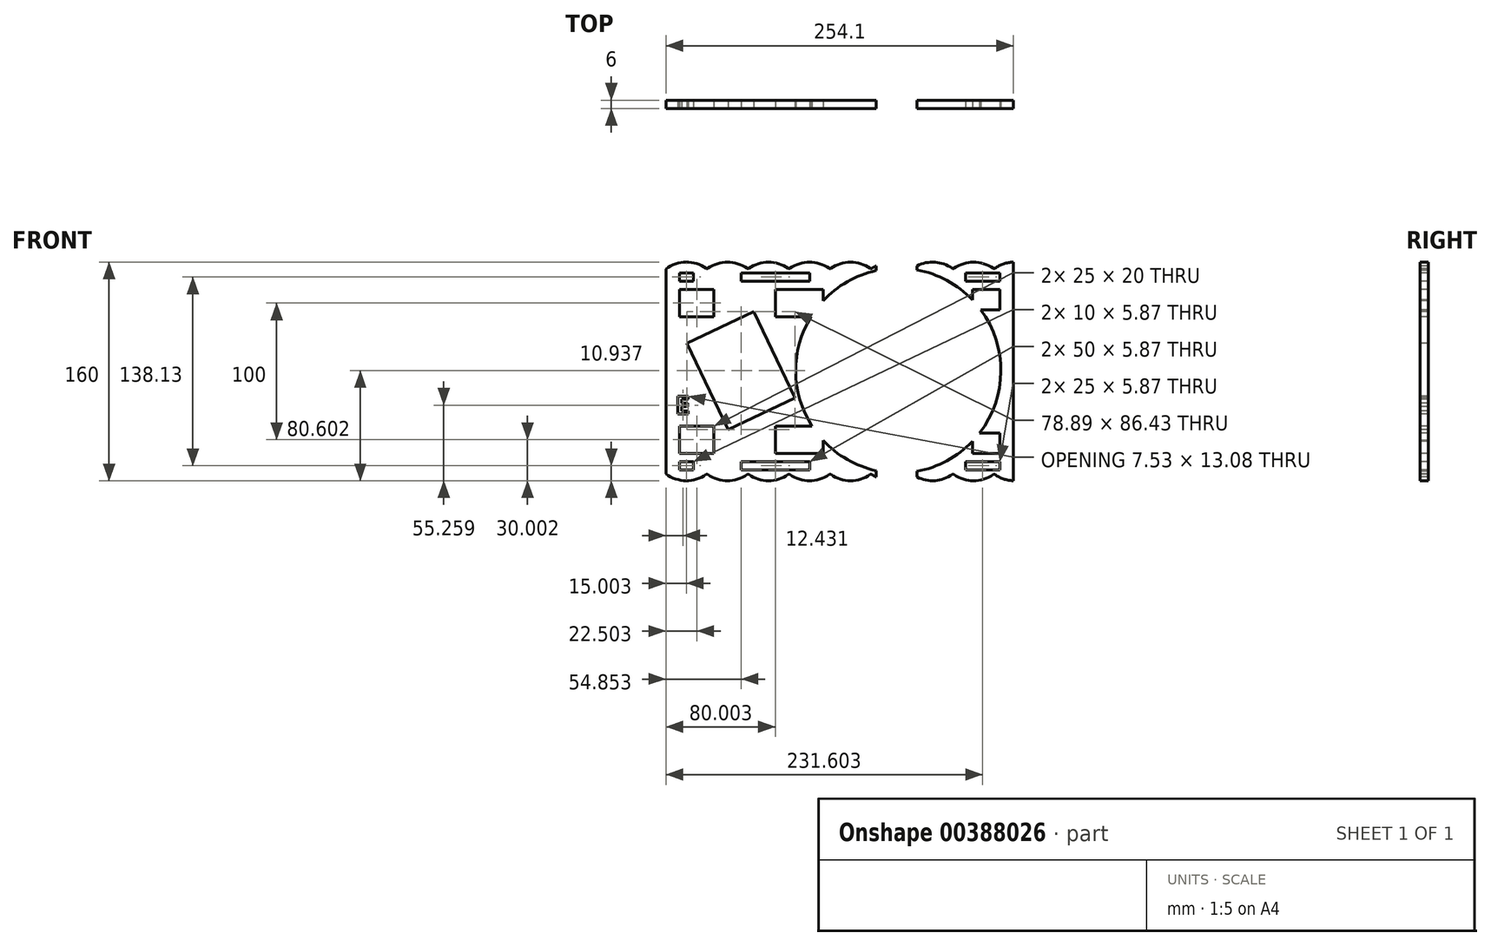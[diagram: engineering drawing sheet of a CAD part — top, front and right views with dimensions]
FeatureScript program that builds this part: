
annotation { "Feature Type Name" : "Feature", "Feature Type Description" : "" }
export const myFeature = defineFeature(function(context is Context, id is Id, definition is map)
    precondition{}
    {
        {
            var Q0;
            Q0=qCreatedBy(makeId("Front.planeOp"),FACE);
            var sketch = newSketch(context, id + "F0", { "sketchPlane" : qUnion([Q0])});
            skCircle(sketch, "E0", {"center": v(28.93, 18.7) * mm, "radius": 75 * mm});
            skPoint(sketch, "E0.first.point", {"position": v(-5.87, 85.13) * mm});
            skPoint(sketch, "E0.second.point", {"position": v(-5.87, -47.74) * mm});
            skPoint(sketch, "E0.second.point.positionSnap0", {"position": v(-5.87, 85.13) * mm});
            skPoint(sketch, "E0.third.point", {"position": v(103.85, 15.25) * mm});
            skLineSegment(sketch, "E1.0", {"start": v(-76.83, 61.9) * mm, "end": v(-125.56, 38.65) * mm});
            skLineSegment(sketch, "E2.0", {"start": v(-46.67, -1.26) * mm, "end": v(-76.83, 61.9) * mm});
            skLineSegment(sketch, "E3.0", {"start": v(-95.4, -24.52) * mm, "end": v(-46.67, -1.26) * mm});
            skLineSegment(sketch, "E4.0", {"start": v(-125.56, 38.65) * mm, "end": v(-95.4, -24.52) * mm});
            skLineSegment(sketch, "E5", {"start": v(-140.97, 101.1) * mm, "end": v(-140.97, 90.01) * mm, "construction": true});
            skLineSegment(sketch, "E6", {"start": v(-133.24, 98.1) * mm, "end": v(-149.42, 98.1) * mm, "construction": true});
            skLineSegment(sketch, "E7.0", {"start": v(76.35, -61.9) * mm, "end": v(117.62, -61.9) * mm, "construction": true});
            skLineSegment(sketch, "E8.0", {"start": v(113.13, 16.1) * mm, "end": v(113.13, -65.37) * mm, "construction": true});
            skLineSegment(sketch, "E9.bottom", {"start": v(-140.97, 98.1) * mm, "end": v(113.13, 98.1) * mm});
            skLineSegment(sketch, "E9.top", {"start": v(-140.97, -61.9) * mm, "end": v(113.13, -61.9) * mm});
            skLineSegment(sketch, "E9.left", {"start": v(-140.97, 98.1) * mm, "end": v(-140.97, -61.9) * mm});
            skLineSegment(sketch, "E9.right", {"start": v(113.13, 98.1) * mm, "end": v(113.13, -61.9) * mm});
            skLineSegment(sketch, "E10", {"start": v(-140.97, 18.1) * mm, "end": v(113.13, 18.1) * mm, "construction": true});
            skLineSegment(sketch, "E11", {"start": v(-76.83, 61.9) * mm, "end": v(-95.4, -24.52) * mm, "construction": true});
            skLineSegment(sketch, "E12", {"start": v(-125.56, 38.65) * mm, "end": v(-46.67, -1.26) * mm, "construction": true});
            skPoint(sketch, "E13", {"position": v(-86.12, 18.7) * mm});
            skCircle(sketch, "E14", {"center": v(-86.12, 18.7) * mm, "radius": 27 * mm, "construction": true});
            skSolve(sketch);
        }
        {
            var Q0;
            Q0=qCreatedBy(makeId("Top.planeOp"),FACE);
            cPlane(context, id + "F1", {"entities" : qUnion([Q0]), "cplaneType" : CPlaneType.OFFSET, "offset" : 61.9 * mm, "oppositeDirection" : true, "width" : 150 * mm, "height" : 150 * mm});
        }
        {
            var Q0;
            Q0 = qSketchRegion(id + "F0", true);
            extrude(context, id + "F2", {"entities" : qUnion([Q0]), "oppositeDirection" : true, "depth" : 6 * mm});
        }
        {
            var Q0;
            Q0=makeQuery(id+"F2.opExtrude","CAP_FACE",FACE,{"disambiguationData":[OSD([sQuery(id+"F0.wireOp",EDGE,"E0"),sQuery(id+"F0.wireOp",EDGE,"E1.0"),sQuery(id+"F0.wireOp",EDGE,"E2.0"),sQuery(id+"F0.wireOp",EDGE,"E3.0"),sQuery(id+"F0.wireOp",EDGE,"E4.0"),sQuery(id+"F0.wireOp",EDGE,"E9.bottom"),sQuery(id+"F0.wireOp",EDGE,"E9.top"),sQuery(id+"F0.wireOp",EDGE,"E9.left"),sQuery(id+"F0.wireOp",EDGE,"E9.right")])],"isStart":true});
            var sketch = newSketch(context, id + "F3", { "sketchPlane" : qUnion([Q0])});
            skLineSegment(sketch, "E15", {"start": v(27.65, 108.76) * mm, "end": v(27.65, -90.8) * mm, "construction": true});
            skLineSegment(sketch, "E16.bottom", {"start": v(12.65, 108.1) * mm, "end": v(42.65, 108.1) * mm});
            skLineSegment(sketch, "E16.top", {"start": v(12.65, 88.1) * mm, "end": v(42.65, 88.1) * mm});
            skLineSegment(sketch, "E16.left", {"start": v(12.65, 108.1) * mm, "end": v(12.65, 88.1) * mm});
            skLineSegment(sketch, "E16.right", {"start": v(42.65, 108.1) * mm, "end": v(42.65, 88.1) * mm});
            skPoint(sketch, "E16.middle", {"position": v(27.65, 98.1) * mm});
            skLineSegment(sketch, "E17", {"start": v(12.65, 88.1) * mm, "end": v(12.65, -89.11) * mm, "construction": true});
            skLineSegment(sketch, "E18", {"start": v(42.65, 88.1) * mm, "end": v(42.65, -87.8) * mm, "construction": true});
            skLineSegment(sketch, "E19.bottom", {"start": v(42.65, -71.9) * mm, "end": v(12.65, -71.9) * mm});
            skLineSegment(sketch, "E19.top", {"start": v(42.65, -51.9) * mm, "end": v(12.65, -51.9) * mm});
            skLineSegment(sketch, "E19.left", {"start": v(42.65, -71.9) * mm, "end": v(42.65, -51.9) * mm});
            skLineSegment(sketch, "E19.right", {"start": v(12.65, -71.9) * mm, "end": v(12.65, -51.9) * mm});
            skPoint(sketch, "E19.middle", {"position": v(27.65, -61.9) * mm});
            skSolve(sketch);
        }
        {
            var Q0;
            Q0 = qSketchRegion(id + "F3", true);
            extrude(context, id + "F4", {"entities" : qUnion([Q0]), "operationType" : NewBodyOperationType.REMOVE, "oppositeDirection" : true, "depth" : 25 * mm});
        }
        {
            var Q0;
            Q0=qCreatedBy(makeId("Front.planeOp"),FACE);
            var sketch = newSketch(context, id + "F5", { "sketchPlane" : qUnion([Q0])});
            skLineSegment(sketch, "E20.bottom", {"start": v(-130.97, 90.1) * mm, "end": v(-120.97, 90.1) * mm});
            skLineSegment(sketch, "E20.top", {"start": v(-130.97, 84.22) * mm, "end": v(-120.97, 84.22) * mm});
            skLineSegment(sketch, "E20.left", {"start": v(-130.97, 90.1) * mm, "end": v(-130.97, 84.22) * mm});
            skLineSegment(sketch, "E20.right", {"start": v(-120.97, 90.1) * mm, "end": v(-120.97, 84.22) * mm});
            skLineSegment(sketch, "E21.bottom", {"start": v(-85.97, 90.1) * mm, "end": v(-35.97, 90.1) * mm});
            skLineSegment(sketch, "E21.top", {"start": v(-85.97, 84.22) * mm, "end": v(-35.97, 84.22) * mm});
            skLineSegment(sketch, "E21.left", {"start": v(-85.97, 90.1) * mm, "end": v(-85.97, 84.22) * mm});
            skLineSegment(sketch, "E21.right", {"start": v(-35.97, 90.1) * mm, "end": v(-35.97, 84.22) * mm});
            skLineSegment(sketch, "E22.bottom", {"start": v(103.13, 84.22) * mm, "end": v(78.13, 84.22) * mm});
            skLineSegment(sketch, "E22.top", {"start": v(103.13, 90.1) * mm, "end": v(78.13, 90.1) * mm});
            skLineSegment(sketch, "E22.left", {"start": v(78.13, 84.22) * mm, "end": v(78.13, 90.1) * mm});
            skLineSegment(sketch, "E22.right", {"start": v(103.13, 84.22) * mm, "end": v(103.13, 90.1) * mm});
            skLineSegment(sketch, "E23", {"start": v(194.11, 90.1) * mm, "end": v(-221.84, 90.1) * mm, "construction": true});
            skPoint(sketch, "E23.endSnap0", {"position": v(-125.97, 90.1) * mm});
            skLineSegment(sketch, "E24.0", {"start": v(-140.97, 98.1) * mm, "end": v(12.65, 98.1) * mm, "construction": true});
            skLineSegment(sketch, "E25.0", {"start": v(19.09, -61.9) * mm, "end": v(-51.4, -61.9) * mm, "construction": true});
            skLineSegment(sketch, "E26", {"start": v(-192.72, 18.1) * mm, "end": v(230.83, 18.1) * mm, "construction": true});
            skLineSegment(sketch, "E27.MirrorCS", {"start": v(103.13, -48.04) * mm, "end": v(103.13, -53.9) * mm});
            skLineSegment(sketch, "E28.MirrorCS", {"start": v(78.13, -48.04) * mm, "end": v(78.13, -53.9) * mm});
            skLineSegment(sketch, "E29.MirrorCS", {"start": v(-130.97, -53.9) * mm, "end": v(-120.97, -53.9) * mm});
            skLineSegment(sketch, "E30.MirrorCS", {"start": v(-35.97, -53.9) * mm, "end": v(-35.97, -48.04) * mm});
            skLineSegment(sketch, "E31.MirrorCS", {"start": v(-85.97, -53.9) * mm, "end": v(-85.97, -48.04) * mm});
            skLineSegment(sketch, "E32.MirrorCS", {"start": v(-130.97, -48.04) * mm, "end": v(-120.97, -48.04) * mm});
            skLineSegment(sketch, "E33.MirrorCS", {"start": v(-130.97, -53.9) * mm, "end": v(-130.97, -48.04) * mm});
            skLineSegment(sketch, "E34.MirrorCS", {"start": v(-120.97, -53.9) * mm, "end": v(-120.97, -48.04) * mm});
            skLineSegment(sketch, "E35.MirrorCS", {"start": v(103.13, -53.9) * mm, "end": v(78.13, -53.9) * mm});
            skLineSegment(sketch, "E36.MirrorCS", {"start": v(-85.97, -53.9) * mm, "end": v(-35.97, -53.9) * mm});
            skLineSegment(sketch, "E37.MirrorCS", {"start": v(194.11, -53.9) * mm, "end": v(-221.84, -53.9) * mm, "construction": true});
            skLineSegment(sketch, "E38.MirrorCS", {"start": v(-140.97, -61.9) * mm, "end": v(12.65, -61.9) * mm, "construction": true});
            skPoint(sketch, "E39.MirrorP", {"position": v(-125.97, -53.9) * mm});
            skLineSegment(sketch, "E40.MirrorCS", {"start": v(103.13, -48.04) * mm, "end": v(78.13, -48.04) * mm});
            skLineSegment(sketch, "E41.MirrorCS", {"start": v(-85.97, -48.04) * mm, "end": v(-35.97, -48.04) * mm});
            skSolve(sketch);
        }
        {
            var Q0;
            Q0 = qSketchRegion(id + "F5", true);
            extrude(context, id + "F6", {"entities" : qUnion([Q0]), "operationType" : NewBodyOperationType.REMOVE, "oppositeDirection" : true, "depth" : 11 * mm});
        }
        {
            var Q0;
            Q0=qCreatedBy(makeId("Front.planeOp"),FACE);
            var sketch = newSketch(context, id + "F7", { "sketchPlane" : qUnion([Q0])});
            skLineSegment(sketch, "E42.0", {"start": v(-140.97, 98.1) * mm, "end": v(-140.97, -61.9) * mm, "construction": true});
            skLineSegment(sketch, "E43.0", {"start": v(113.13, 98.1) * mm, "end": v(113.13, -61.9) * mm, "construction": true});
            skLineSegment(sketch, "E44", {"start": v(-140.97, 93.1) * mm, "end": v(113.13, 93.1) * mm, "construction": true});
            skArc(sketch, "E45", {"start": v(-111.54, 93.51) * mm, "mid": v(-126.32, 98.09) * mm, "end": v(-140.97, 93.1) * mm});
            skLineSegment(sketch, "E46.0.0", {"start": v(-140.97, -61.9) * mm, "end": v(12.65, -61.9) * mm, "construction": true});
            skLineSegment(sketch, "E46.0.1", {"start": v(12.65, -61.9) * mm, "end": v(12.65, -54.52) * mm, "construction": true});
            skArc(sketch, "E46.0.2", {"start": v(12.65, -54.52) * mm, "mid": v(-46.07, 18.7) * mm, "end": v(12.65, 91.9) * mm, "construction": true});
            skLineSegment(sketch, "E46.0.3", {"start": v(12.65, 91.9) * mm, "end": v(12.65, 98.1) * mm, "construction": true});
            skLineSegment(sketch, "E46.0.4", {"start": v(12.65, 98.1) * mm, "end": v(-140.97, 98.1) * mm, "construction": true});
            skArc(sketch, "E47.1.0.0", {"start": v(-81.54, 93.51) * mm, "mid": v(-95.97, 98.1) * mm, "end": v(-110.4, 93.51) * mm});
            skArc(sketch, "E47.2.0.0", {"start": v(-51.54, 93.51) * mm, "mid": v(-65.97, 98.1) * mm, "end": v(-80.4, 93.51) * mm});
            skArc(sketch, "E47.3.0.0", {"start": v(-21.54, 93.51) * mm, "mid": v(-35.97, 98.1) * mm, "end": v(-50.4, 93.51) * mm});
            skArc(sketch, "E47.4.0.0", {"start": v(8.46, 93.51) * mm, "mid": v(-5.97, 98.1) * mm, "end": v(-20.4, 93.51) * mm});
            skArc(sketch, "E47.5.0.0", {"start": v(38.46, 93.51) * mm, "mid": v(24.03, 98.1) * mm, "end": v(9.6, 93.51) * mm});
            skArc(sketch, "E47.6.0.0", {"start": v(68.46, 93.51) * mm, "mid": v(54.03, 98.1) * mm, "end": v(39.6, 93.51) * mm});
            skArc(sketch, "E47.7.0.0", {"start": v(98.46, 93.51) * mm, "mid": v(84.03, 98.1) * mm, "end": v(69.6, 93.51) * mm});
            skArc(sketch, "E47.8.0.0", {"start": v(129.03, 93.1) * mm, "mid": v(114.39, 98.09) * mm, "end": v(99.6, 93.51) * mm});
            skArc(sketch, "E47.9.0.0", {"start": v(159.03, 93.1) * mm, "mid": v(144.03, 98.1) * mm, "end": v(129.03, 93.1) * mm});
            skLineSegment(sketch, "E47.direction1", {"start": v(-125.97, 73.1) * mm, "end": v(-95.97, 73.1) * mm, "construction": true});
            skPoint(sketch, "E48.visualSharp", {"position": v(-110.97, 93.1) * mm});
            skArc(sketch, "E48.filletArc", {"start": v(-111.54, 93.51) * mm, "mid": v(-110.97, 93.33) * mm, "end": v(-110.4, 93.51) * mm});
            skPoint(sketch, "E49.visualSharp", {"position": v(-80.97, 93.1) * mm});
            skArc(sketch, "E49.filletArc", {"start": v(-81.54, 93.51) * mm, "mid": v(-80.97, 93.33) * mm, "end": v(-80.4, 93.51) * mm});
            skPoint(sketch, "E50.visualSharp", {"position": v(-50.97, 93.1) * mm});
            skArc(sketch, "E50.filletArc", {"start": v(-51.54, 93.51) * mm, "mid": v(-50.97, 93.33) * mm, "end": v(-50.4, 93.51) * mm});
            skPoint(sketch, "E51.visualSharp", {"position": v(9.03, 93.1) * mm});
            skArc(sketch, "E51.filletArc", {"start": v(8.46, 93.51) * mm, "mid": v(9.03, 93.33) * mm, "end": v(9.6, 93.51) * mm});
            skPoint(sketch, "E52.visualSharp", {"position": v(-20.97, 93.1) * mm});
            skArc(sketch, "E52.filletArc", {"start": v(-21.54, 93.51) * mm, "mid": v(-20.97, 93.33) * mm, "end": v(-20.4, 93.51) * mm});
            skPoint(sketch, "E53.visualSharp", {"position": v(39.03, 93.1) * mm});
            skArc(sketch, "E53.filletArc", {"start": v(38.46, 93.51) * mm, "mid": v(39.03, 93.33) * mm, "end": v(39.6, 93.51) * mm});
            skPoint(sketch, "E54.visualSharp", {"position": v(69.03, 93.1) * mm});
            skArc(sketch, "E54.filletArc", {"start": v(68.46, 93.51) * mm, "mid": v(69.03, 93.33) * mm, "end": v(69.6, 93.51) * mm});
            skPoint(sketch, "E55.visualSharp", {"position": v(99.03, 93.1) * mm});
            skArc(sketch, "E55.filletArc", {"start": v(98.46, 93.51) * mm, "mid": v(99.03, 93.33) * mm, "end": v(99.6, 93.51) * mm});
            skLineSegment(sketch, "E56", {"start": v(-140.97, 93.1) * mm, "end": v(-149.28, 93.1) * mm});
            skLineSegment(sketch, "E57", {"start": v(-149.28, 93.1) * mm, "end": v(-149.28, 104.87) * mm});
            skLineSegment(sketch, "E58", {"start": v(-149.28, 104.87) * mm, "end": v(159, 104.87) * mm});
            skLineSegment(sketch, "E59", {"start": v(159, 104.87) * mm, "end": v(159.03, 93.1) * mm});
            skLineSegment(sketch, "E60", {"start": v(-140.97, 18.1) * mm, "end": v(179.08, 18.1) * mm, "construction": true});
            skArc(sketch, "E61.MirrorCS", {"start": v(68.46, -57.33) * mm, "mid": v(69.03, -57.14) * mm, "end": v(69.6, -57.33) * mm});
            skLineSegment(sketch, "E62.MirrorCS", {"start": v(12.65, -55.72) * mm, "end": v(12.65, -61.9) * mm, "construction": true});
            skArc(sketch, "E63.MirrorCS", {"start": v(8.46, -57.33) * mm, "mid": v(9.03, -57.14) * mm, "end": v(9.6, -57.33) * mm});
            skArc(sketch, "E64.MirrorCS", {"start": v(38.46, -57.33) * mm, "mid": v(24.03, -61.9) * mm, "end": v(9.6, -57.33) * mm});
            skArc(sketch, "E65.MirrorCS", {"start": v(-51.54, -57.33) * mm, "mid": v(-50.97, -57.14) * mm, "end": v(-50.4, -57.33) * mm});
            skArc(sketch, "E66.MirrorCS", {"start": v(38.46, -57.33) * mm, "mid": v(39.03, -57.14) * mm, "end": v(39.6, -57.33) * mm});
            skArc(sketch, "E67.MirrorCS", {"start": v(98.46, -57.33) * mm, "mid": v(84.03, -61.9) * mm, "end": v(69.6, -57.33) * mm});
            skArc(sketch, "E68.MirrorCS", {"start": v(98.46, -57.33) * mm, "mid": v(99.03, -57.14) * mm, "end": v(99.6, -57.33) * mm});
            skArc(sketch, "E69.MirrorCS", {"start": v(-111.54, -57.33) * mm, "mid": v(-110.97, -57.14) * mm, "end": v(-110.4, -57.33) * mm});
            skArc(sketch, "E70.MirrorCS", {"start": v(-21.54, -57.33) * mm, "mid": v(-20.97, -57.14) * mm, "end": v(-20.4, -57.33) * mm});
            skArc(sketch, "E71.MirrorCS", {"start": v(-81.54, -57.33) * mm, "mid": v(-80.97, -57.14) * mm, "end": v(-80.4, -57.33) * mm});
            skArc(sketch, "E72.MirrorCS", {"start": v(-21.54, -57.33) * mm, "mid": v(-35.97, -61.9) * mm, "end": v(-50.4, -57.33) * mm});
            skArc(sketch, "E73.MirrorCS", {"start": v(-51.54, -57.33) * mm, "mid": v(-65.97, -61.9) * mm, "end": v(-80.4, -57.33) * mm});
            skArc(sketch, "E74.MirrorCS", {"start": v(8.46, -57.33) * mm, "mid": v(-5.97, -61.9) * mm, "end": v(-20.4, -57.33) * mm});
            skLineSegment(sketch, "E75.MirrorCS", {"start": v(-140.97, -56.9) * mm, "end": v(-149.28, -56.9) * mm});
            skArc(sketch, "E76.MirrorCS", {"start": v(-111.54, -57.33) * mm, "mid": v(-126.32, -61.9) * mm, "end": v(-140.97, -56.9) * mm});
            skLineSegment(sketch, "E77.MirrorCS", {"start": v(12.65, -61.9) * mm, "end": v(-140.97, -61.9) * mm, "construction": true});
            skArc(sketch, "E78.MirrorCS", {"start": v(-81.54, -57.33) * mm, "mid": v(-95.97, -61.9) * mm, "end": v(-110.4, -57.33) * mm});
            skLineSegment(sketch, "E79.MirrorCS", {"start": v(-149.28, -56.9) * mm, "end": v(-149.28, -68.69) * mm});
            skLineSegment(sketch, "E80.MirrorCS", {"start": v(-125.97, -36.9) * mm, "end": v(-95.97, -36.9) * mm, "construction": true});
            skLineSegment(sketch, "E81.MirrorCS", {"start": v(159, -68.69) * mm, "end": v(159.03, -56.9) * mm});
            skArc(sketch, "E82.MirrorCS", {"start": v(129.03, -56.9) * mm, "mid": v(114.39, -61.9) * mm, "end": v(99.6, -57.33) * mm});
            skArc(sketch, "E83.MirrorCS", {"start": v(68.46, -57.33) * mm, "mid": v(54.03, -61.9) * mm, "end": v(39.6, -57.33) * mm});
            skLineSegment(sketch, "E84.MirrorCS", {"start": v(-140.97, -61.9) * mm, "end": v(-140.97, 98.1) * mm, "construction": true});
            skLineSegment(sketch, "E85.MirrorCS", {"start": v(-140.97, -56.9) * mm, "end": v(113.13, -56.9) * mm, "construction": true});
            skPoint(sketch, "E86.MirrorP", {"position": v(9.03, -56.9) * mm});
            skLineSegment(sketch, "E87.MirrorCS", {"start": v(-149.28, -68.69) * mm, "end": v(159, -68.69) * mm});
            skPoint(sketch, "E88.MirrorP", {"position": v(-50.97, -56.9) * mm});
            skLineSegment(sketch, "E89.MirrorCS", {"start": v(113.13, -61.9) * mm, "end": v(113.13, 98.1) * mm, "construction": true});
            skPoint(sketch, "E90.MirrorP", {"position": v(-80.97, -56.9) * mm});
            skArc(sketch, "E91.MirrorCS", {"start": v(159.03, -56.9) * mm, "mid": v(144.03, -61.9) * mm, "end": v(129.03, -56.9) * mm});
            skPoint(sketch, "E92.MirrorP", {"position": v(69.03, -56.9) * mm});
            skArc(sketch, "E93.MirrorCS", {"start": v(12.65, 90.7) * mm, "mid": v(-46.07, 17.5) * mm, "end": v(12.65, -55.72) * mm, "construction": true});
            skPoint(sketch, "E94.MirrorP", {"position": v(-110.97, -56.9) * mm});
            skPoint(sketch, "E95.MirrorP", {"position": v(39.03, -56.9) * mm});
            skPoint(sketch, "E96.MirrorP", {"position": v(99.03, -56.9) * mm});
            skPoint(sketch, "E97.MirrorP", {"position": v(-20.97, -56.9) * mm});
            skLineSegment(sketch, "E98.bottom", {"start": v(-130.97, 78.1) * mm, "end": v(-105.97, 78.1) * mm});
            skLineSegment(sketch, "E98.top", {"start": v(-130.97, 58.1) * mm, "end": v(-105.97, 58.1) * mm});
            skLineSegment(sketch, "E98.left", {"start": v(-130.97, 78.1) * mm, "end": v(-130.97, 58.1) * mm});
            skLineSegment(sketch, "E98.right", {"start": v(-105.97, 78.1) * mm, "end": v(-105.97, 58.1) * mm});
            skLineSegment(sketch, "E99.bottom", {"start": v(-60.97, 78.1) * mm, "end": v(-25.97, 78.1) * mm});
            skLineSegment(sketch, "E99.top", {"start": v(-60.97, 58.1) * mm, "end": v(-25.97, 58.1) * mm});
            skLineSegment(sketch, "E99.left", {"start": v(-60.97, 78.1) * mm, "end": v(-60.97, 58.1) * mm});
            skLineSegment(sketch, "E99.right", {"start": v(-25.97, 78.1) * mm, "end": v(-25.97, 58.1) * mm});
            skLineSegment(sketch, "E100.bottom", {"start": v(103.13, 78.1) * mm, "end": v(83.13, 78.1) * mm});
            skLineSegment(sketch, "E100.top", {"start": v(103.13, 63.1) * mm, "end": v(83.13, 63.1) * mm});
            skLineSegment(sketch, "E100.left", {"start": v(103.13, 78.1) * mm, "end": v(103.13, 63.1) * mm});
            skLineSegment(sketch, "E100.right", {"start": v(83.13, 78.1) * mm, "end": v(83.13, 63.1) * mm});
            skLineSegment(sketch, "E101.MirrorCS", {"start": v(103.13, -41.9) * mm, "end": v(103.13, -26.9) * mm});
            skLineSegment(sketch, "E102.MirrorCS", {"start": v(103.13, -26.9) * mm, "end": v(83.13, -26.9) * mm});
            skLineSegment(sketch, "E103.MirrorCS", {"start": v(83.13, -41.9) * mm, "end": v(83.13, -26.9) * mm});
            skLineSegment(sketch, "E104.MirrorCS", {"start": v(103.13, -41.9) * mm, "end": v(83.13, -41.9) * mm});
            skLineSegment(sketch, "E105.MirrorCS", {"start": v(-25.97, -41.9) * mm, "end": v(-25.97, -21.9) * mm});
            skLineSegment(sketch, "E106.MirrorCS", {"start": v(-60.97, -41.9) * mm, "end": v(-25.97, -41.9) * mm});
            skLineSegment(sketch, "E107.MirrorCS", {"start": v(-60.97, -21.9) * mm, "end": v(-25.97, -21.9) * mm});
            skLineSegment(sketch, "E108.MirrorCS", {"start": v(-60.97, -41.9) * mm, "end": v(-60.97, -21.9) * mm});
            skLineSegment(sketch, "E109.MirrorCS", {"start": v(-105.97, -41.9) * mm, "end": v(-105.97, -21.9) * mm});
            skLineSegment(sketch, "E110.MirrorCS", {"start": v(-130.97, -21.9) * mm, "end": v(-105.97, -21.9) * mm});
            skLineSegment(sketch, "E111.MirrorCS", {"start": v(-130.97, -41.9) * mm, "end": v(-130.97, -21.9) * mm});
            skLineSegment(sketch, "E112.MirrorCS", {"start": v(-130.97, -41.9) * mm, "end": v(-105.97, -41.9) * mm});
            skSolve(sketch);
        }
        {
            var Q0;
            Q0 = qSketchRegion(id + "F7", true);
            extrude(context, id + "F8", {"entities" : qUnion([Q0]), "operationType" : NewBodyOperationType.REMOVE, "oppositeDirection" : true, "depth" : 25 * mm});
        }
        {
            var Q0;
            {var subQ0=sQuery(id+"F0.wireOp",EDGE,"E2.0");var subQ1=sQuery(id+"F0.wireOp",EDGE,"E1.0");var subQ2=sQuery(id+"F0.wireOp",EDGE,"E3.0");var subQ3=sQuery(id+"F0.wireOp",EDGE,"E0");var subQ4=sQuery(id+"F0.wireOp",EDGE,"E4.0");var subQ5=sQuery(id+"F0.wireOp",EDGE,"E9.bottom");var subQ6=sQuery(id+"F0.wireOp",EDGE,"E9.top");var subQ7=sQuery(id+"F0.wireOp",EDGE,"E9.left");Q0=makeQuery(id+"F4.boolean.opBoolean","SPLIT",FACE,{"disambiguationData":[TD([makeQuery(id+"F2.opExtrude","SWEPT_FACE",FACE,{"disambiguationData":[OSD([subQ1])]})])],"derivedFrom":makeQuery(id+"F2.opExtrude","CAP_FACE",FACE,{"disambiguationData":[OSD([subQ3,subQ1,subQ0,subQ2,subQ4,subQ5,subQ6,subQ7,sQuery(id+"F0.wireOp",EDGE,"E9.right")])],"isStart":true})});}
            var sketch = newSketch(context, id + "F9", { "sketchPlane" : qUnion([Q0])});
            skText(sketch, "E113", { "text": "E", "fontName": "OpenSans-Bold.ttf"});
            const initialGuessF9  = {"E113": [-0.13395, -0.01319, 1, 0, 0.01319]};
            skSetInitialGuess(sketch, initialGuessF9);
            skSolve(sketch);
        }
        {
            var Q0;
            Q0 = qSketchRegion(id + "F9", true);
            extrude(context, id + "F10", {"entities" : qUnion([Q0]), "operationType" : NewBodyOperationType.REMOVE, "oppositeDirection" : true, "depth" : 25 * mm});
        }
    });
